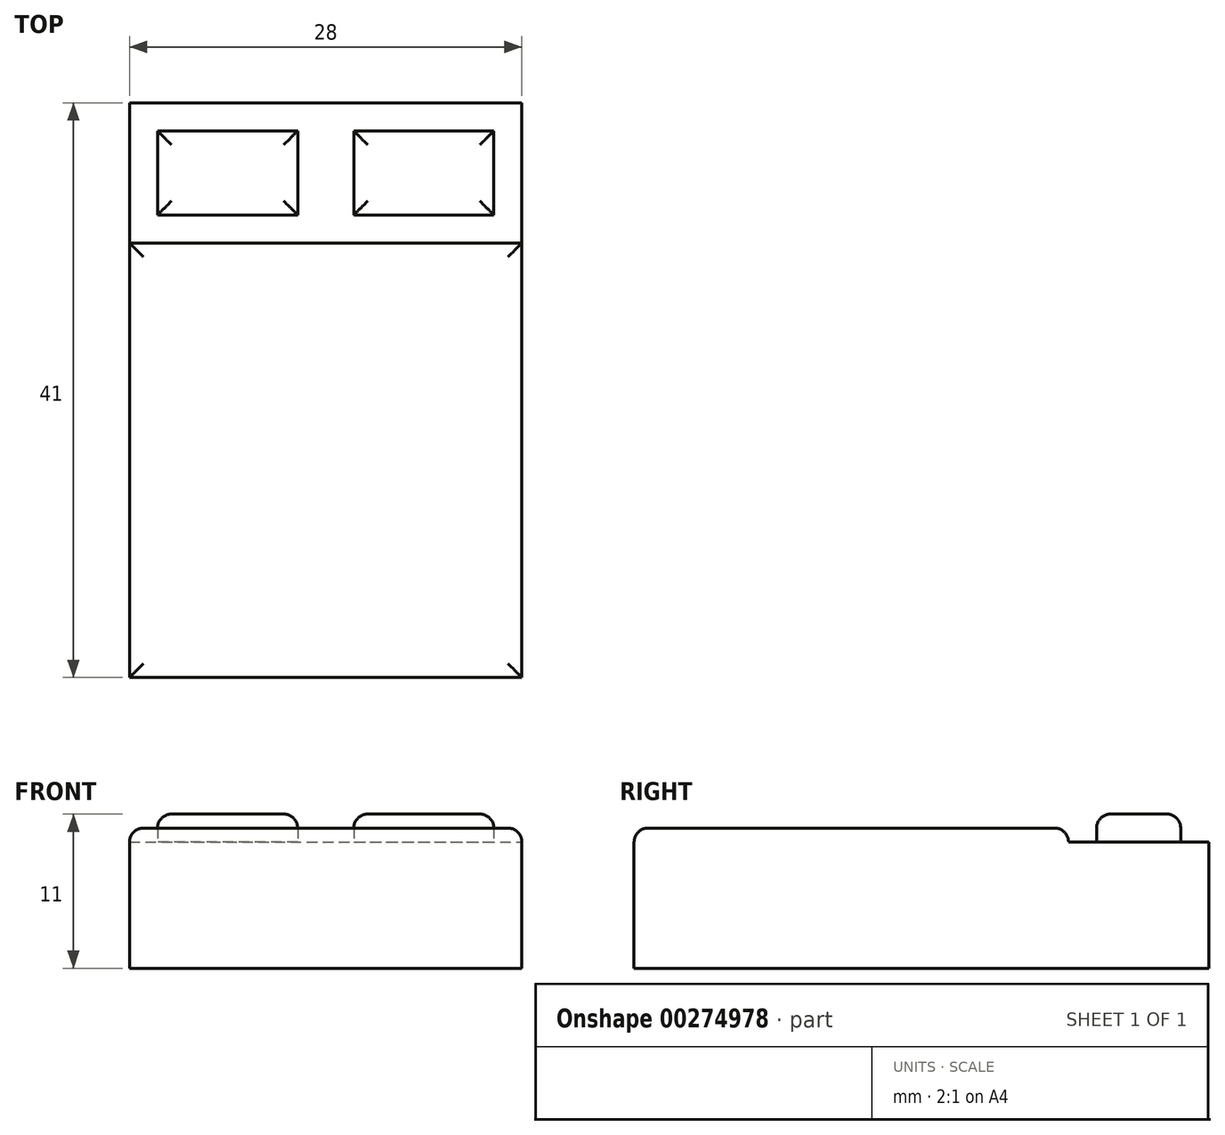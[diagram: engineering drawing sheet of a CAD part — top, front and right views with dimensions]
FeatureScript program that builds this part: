
annotation { "Feature Type Name" : "Feature", "Feature Type Description" : "" }
export const myFeature = defineFeature(function(context is Context, id is Id, definition is map)
    precondition{}
    {
        {
            var Q0;
            Q0=qCreatedBy(makeId("Top.planeOp"),FACE);
            var sketch = newSketch(context, id + "F0", { "sketchPlane" : qUnion([Q0])});
            skLineSegment(sketch, "E0.bottom", {"start": v(0, 0) * mm, "end": v(28, 0) * mm});
            skLineSegment(sketch, "E0.top", {"start": v(0, 41) * mm, "end": v(28, 41) * mm});
            skLineSegment(sketch, "E0.left", {"start": v(0, 0) * mm, "end": v(0, 41) * mm});
            skLineSegment(sketch, "E0.right", {"start": v(28, 0) * mm, "end": v(28, 41) * mm});
            skLineSegment(sketch, "E1", {"start": v(0, 31) * mm, "end": v(28, 31) * mm});
            skLineSegment(sketch, "E2.bottom", {"start": v(12, 39) * mm, "end": v(2, 39) * mm});
            skLineSegment(sketch, "E2.top", {"start": v(12, 33) * mm, "end": v(2, 33) * mm});
            skLineSegment(sketch, "E2.left", {"start": v(12, 39) * mm, "end": v(12, 33) * mm});
            skLineSegment(sketch, "E2.right", {"start": v(2, 39) * mm, "end": v(2, 33) * mm});
            skLineSegment(sketch, "E3.bottom", {"start": v(16, 39) * mm, "end": v(26, 39) * mm});
            skLineSegment(sketch, "E3.top", {"start": v(16, 33) * mm, "end": v(26, 33) * mm});
            skLineSegment(sketch, "E3.left", {"start": v(16, 39) * mm, "end": v(16, 33) * mm});
            skLineSegment(sketch, "E3.right", {"start": v(26, 39) * mm, "end": v(26, 33) * mm});
            skSolve(sketch);
        }
        {
            var Q0;
            {var subQ0=sQuery(id+"F0.wireOp",EDGE,"E0.top");Q0=makeQuery(id+"F0.imprint","IMPRINT",FACE,{"disambiguationData":[TD([[makeQuery(id+"F0.imprint","IMPRINT",EDGE,{"derivedFrom":subQ0}),-1.0]])]});}
            var Q1;
            Q1=makeQuery(id+"F0.imprint","IMPRINT",FACE,{"disambiguationData":[TD([[makeQuery(id+"F0.imprint","IMPRINT",EDGE,{"derivedFrom":sQuery(id+"F0.wireOp",EDGE,"E2.bottom")}),1.0]])]});
            var Q2;
            Q2=makeQuery(id+"F0.imprint","IMPRINT",FACE,{"disambiguationData":[TD([[makeQuery(id+"F0.imprint","IMPRINT",EDGE,{"derivedFrom":sQuery(id+"F0.wireOp",EDGE,"E3.bottom")}),-1.0]])]});
            var Q3;
            {var subQ0=sQuery(id+"F0.wireOp",EDGE,"E0.bottom");Q3=makeQuery(id+"F0.imprint","IMPRINT",FACE,{"disambiguationData":[TD([[makeQuery(id+"F0.imprint","IMPRINT",EDGE,{"derivedFrom":subQ0}),1.0]])]});}
            extrude(context, id + "F1", {"entities" : qUnion([Q0, Q1, Q2, Q3]), "oppositeDirection" : true, "depth" : 9 * mm});
        }
        {
            var Q0;
            {var subQ0=sQuery(id+"F0.wireOp",EDGE,"E0.bottom");Q0=makeQuery(id+"F0.imprint","IMPRINT",FACE,{"disambiguationData":[TD([[makeQuery(id+"F0.imprint","IMPRINT",EDGE,{"derivedFrom":subQ0}),1.0]])]});}
            extrude(context, id + "F2", {"entities" : qUnion([Q0]), "operationType" : NewBodyOperationType.ADD, "depth" : 1 * mm});
        }
        {
            var Q0;
            Q0=makeQuery(id+"F0.imprint","IMPRINT",FACE,{"disambiguationData":[TD([[makeQuery(id+"F0.imprint","IMPRINT",EDGE,{"derivedFrom":sQuery(id+"F0.wireOp",EDGE,"E2.bottom")}),1.0]])]});
            var Q1;
            Q1=makeQuery(id+"F0.imprint","IMPRINT",FACE,{"disambiguationData":[TD([[makeQuery(id+"F0.imprint","IMPRINT",EDGE,{"derivedFrom":sQuery(id+"F0.wireOp",EDGE,"E3.bottom")}),-1.0]])]});
            extrude(context, id + "F3", {"entities" : qUnion([Q0, Q1]), "operationType" : NewBodyOperationType.ADD, "depth" : 2 * mm});
        }
        {
            var Q0;
            Q0=makeQuery(id+"F3.opExtrude","CAP_FACE",FACE,{"disambiguationData":[OSD([sQuery(id+"F0.wireOp",EDGE,"E2.bottom"),sQuery(id+"F0.wireOp",EDGE,"E2.top"),sQuery(id+"F0.wireOp",EDGE,"E2.left"),sQuery(id+"F0.wireOp",EDGE,"E2.right")])],"isStart":false});
            var Q1;
            Q1=makeQuery(id+"F3.opExtrude","CAP_FACE",FACE,{"disambiguationData":[OSD([sQuery(id+"F0.wireOp",EDGE,"E3.bottom"),sQuery(id+"F0.wireOp",EDGE,"E3.top"),sQuery(id+"F0.wireOp",EDGE,"E3.left"),sQuery(id+"F0.wireOp",EDGE,"E3.right")])],"isStart":false});
            var Q2;
            Q2=makeQuery(id+"F2.opExtrude","CAP_FACE",FACE,{"disambiguationData":[OSD([sQuery(id+"F0.wireOp",EDGE,"E0.bottom"),sQuery(id+"F0.wireOp",EDGE,"E0.left"),sQuery(id+"F0.wireOp",EDGE,"E0.right"),sQuery(id+"F0.wireOp",EDGE,"E1")])],"isStart":false});
            fillet(context, id + "F4", {"entities" : qUnion([Q0, Q1, Q2]), "radius" : 1 * mm, "tangentPropagation" : true, "allowEdgeOverflow" : false});
        }
    });
